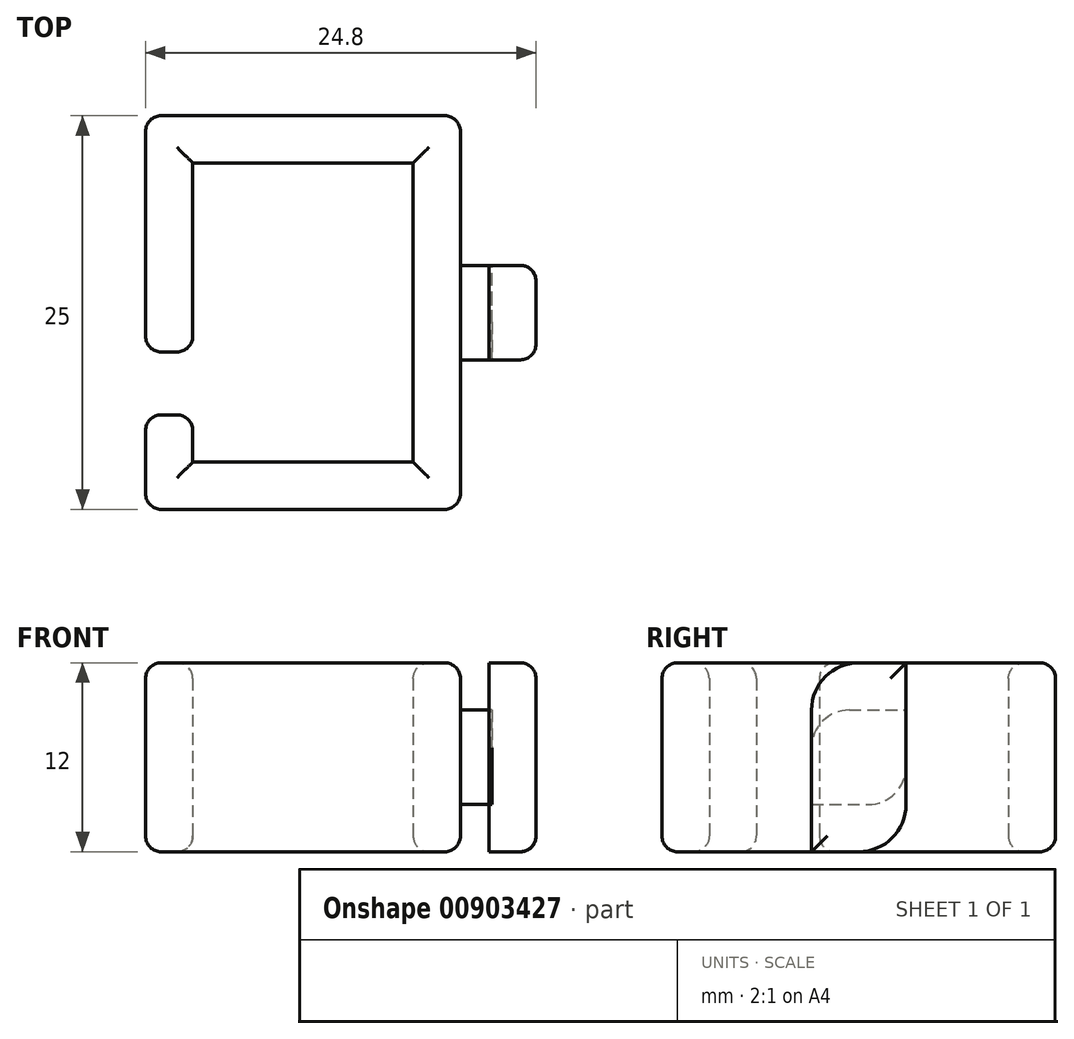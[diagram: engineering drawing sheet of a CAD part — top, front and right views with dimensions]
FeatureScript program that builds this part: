
annotation { "Feature Type Name" : "Feature", "Feature Type Description" : "" }
export const myFeature = defineFeature(function(context is Context, id is Id, definition is map)
    precondition{}
    {
        {
            var Q0;
            Q0=qCreatedBy(makeId("Right.planeOp"),FACE);
            var sketch = newSketch(context, id + "F0", { "sketchPlane" : qUnion([Q0])});
            skLineSegment(sketch, "E0.bottom", {"start": v(-3, -3) * mm, "end": v(3, -3) * mm});
            skLineSegment(sketch, "E0.top", {"start": v(-3, 3) * mm, "end": v(3, 3) * mm});
            skLineSegment(sketch, "E0.left", {"start": v(-3, -3) * mm, "end": v(-3, 3) * mm});
            skLineSegment(sketch, "E0.right", {"start": v(3, -3) * mm, "end": v(3, 3) * mm});
            skPoint(sketch, "E0.middle", {"position": v(0, 0) * mm});
            skLineSegment(sketch, "E1.bottom", {"start": v(-12.5, 6) * mm, "end": v(12.5, 6) * mm});
            skLineSegment(sketch, "E1.top", {"start": v(-12.5, -6) * mm, "end": v(12.5, -6) * mm});
            skLineSegment(sketch, "E1.left", {"start": v(-12.5, 6) * mm, "end": v(-12.5, -6) * mm});
            skLineSegment(sketch, "E1.right", {"start": v(12.5, 6) * mm, "end": v(12.5, -6) * mm});
            skLineSegment(sketch, "E2.bottom", {"start": v(-3, 6) * mm, "end": v(3, 6) * mm});
            skLineSegment(sketch, "E2.top", {"start": v(-3, -6) * mm, "end": v(3, -6) * mm});
            skLineSegment(sketch, "E2.left", {"start": v(-3, 6) * mm, "end": v(-3, -6) * mm});
            skLineSegment(sketch, "E2.right", {"start": v(3, 6) * mm, "end": v(3, -6) * mm});
            skLineSegment(sketch, "E3.bottom", {"start": v(9.5, 6) * mm, "end": v(-9.5, 6) * mm});
            skLineSegment(sketch, "E3.top", {"start": v(9.5, -6) * mm, "end": v(-9.5, -6) * mm});
            skLineSegment(sketch, "E3.left", {"start": v(9.5, 6) * mm, "end": v(9.5, -6) * mm});
            skLineSegment(sketch, "E3.right", {"start": v(-9.5, 6) * mm, "end": v(-9.5, -6) * mm});
            skSolve(sketch);
        }
        {
            var Q0;
            {var subQ2=sQuery(id+"F0.wireOp",EDGE,"E1.left");Q0=makeQuery(id+"F0.imprint","IMPRINT",FACE,{"disambiguationData":[TD([[makeQuery(id+"F0.imprint","IMPRINT",EDGE,{"derivedFrom":subQ2}),1.0]])]});}
            var Q1;
            {var subQ0=sQuery(id+"F0.wireOp",EDGE,"E0.top");Q1=makeQuery(id+"F0.imprint","IMPRINT",FACE,{"disambiguationData":[TD([[makeQuery(id+"F0.imprint","IMPRINT",EDGE,{"derivedFrom":subQ0}),1.0]])]});}
            var Q2;
            {var subQ0=sQuery(id+"F0.wireOp",EDGE,"E0.bottom");Q2=makeQuery(id+"F0.imprint","IMPRINT",FACE,{"disambiguationData":[TD([[makeQuery(id+"F0.imprint","IMPRINT",EDGE,{"derivedFrom":subQ0}),-1.0]])]});}
            var Q3;
            Q3=makeQuery(id+"F0.imprint","IMPRINT",FACE,{"disambiguationData":[TD([[makeQuery(id+"F0.imprint","IMPRINT",EDGE,{"derivedFrom":sQuery(id+"F0.wireOp",EDGE,"E0.bottom")}),1.0]])]});
            var Q4;
            {var subQ0=sQuery(id+"F0.wireOp",EDGE,"E1.right");Q4=makeQuery(id+"F0.imprint","IMPRINT",FACE,{"disambiguationData":[TD([[makeQuery(id+"F0.imprint","IMPRINT",EDGE,{"derivedFrom":subQ0}),-1.0]])]});}
            var Q5;
            {var subQ1=sQuery(id+"F0.wireOp",EDGE,"E0.left");Q5=makeQuery(id+"F0.imprint","IMPRINT",FACE,{"disambiguationData":[TD([[makeQuery(id+"F0.imprint","IMPRINT",EDGE,{"derivedFrom":subQ1}),1.0]])]});}
            var Q6;
            {var subQ6=sQuery(id+"F0.wireOp",EDGE,"E0.right");Q6=makeQuery(id+"F0.imprint","IMPRINT",FACE,{"disambiguationData":[TD([[makeQuery(id+"F0.imprint","IMPRINT",EDGE,{"derivedFrom":subQ6}),-1.0]])]});}
            extrude(context, id + "F1", {"entities" : qUnion([Q0, Q1, Q2, Q3, Q4, Q5, Q6]), "depth" : -3 * mm, "offsetDistance" : 25 * mm});
        }
        {
            var Q0;
            {var subQ0=sQuery(id+"F0.wireOp",EDGE,"E0.top");Q0=makeQuery(id+"F0.imprint","IMPRINT",FACE,{"disambiguationData":[TD([[makeQuery(id+"F0.imprint","IMPRINT",EDGE,{"derivedFrom":subQ0}),1.0]])]});}
            var Q1;
            Q1=makeQuery(id+"F0.imprint","IMPRINT",FACE,{"disambiguationData":[TD([[makeQuery(id+"F0.imprint","IMPRINT",EDGE,{"derivedFrom":sQuery(id+"F0.wireOp",EDGE,"E0.bottom")}),1.0]])]});
            var Q2;
            {var subQ0=sQuery(id+"F0.wireOp",EDGE,"E0.bottom");Q2=makeQuery(id+"F0.imprint","IMPRINT",FACE,{"disambiguationData":[TD([[makeQuery(id+"F0.imprint","IMPRINT",EDGE,{"derivedFrom":subQ0}),-1.0]])]});}
            extrude(context, id + "F2", {"entities" : qUnion([Q0, Q1, Q2]), "depth" : 4.8 * mm, "offsetDistance" : 25 * mm, "hasSecondDirection" : true, "secondDirectionOppositeDirection" : true, "secondDirectionDepth" : -1.8 * mm});
        }
        {
            var Q0;
            Q0=makeQuery(id+"F0.imprint","IMPRINT",FACE,{"disambiguationData":[TD([[makeQuery(id+"F0.imprint","IMPRINT",EDGE,{"derivedFrom":sQuery(id+"F0.wireOp",EDGE,"E0.bottom")}),1.0]])]});
            extrude(context, id + "F3", {"entities" : qUnion([Q0]), "depth" : 2 * mm, "offsetDistance" : 25 * mm});
        }
        {
            var Q0;
            {var subQ0=sQuery(id+"F0.wireOp",EDGE,"E1.right");Q0=makeQuery(id+"F0.imprint","IMPRINT",FACE,{"disambiguationData":[TD([[makeQuery(id+"F0.imprint","IMPRINT",EDGE,{"derivedFrom":subQ0}),-1.0]])]});}
            var Q1;
            {var subQ2=sQuery(id+"F0.wireOp",EDGE,"E1.left");Q1=makeQuery(id+"F0.imprint","IMPRINT",FACE,{"disambiguationData":[TD([[makeQuery(id+"F0.imprint","IMPRINT",EDGE,{"derivedFrom":subQ2}),1.0]])]});}
            extrude(context, id + "F4", {"entities" : qUnion([Q0, Q1]), "operationType" : NewBodyOperationType.ADD, "depth" : -20 * mm, "offsetDistance" : 25 * mm, "hasSecondDirection" : true, "secondDirectionOppositeDirection" : true, "secondDirectionDepth" : 3 * mm});
        }
        {
            var Q0;
            Q0=makeQuery(id+"F2.opExtrude","SWEPT_EDGE",EDGE,{"disambiguationData":[OSD([sQuery(id+"F0.wireOp",EDGE,"E1.bottom"),sQuery(id+"F0.wireOp",EDGE,"E2.left")])]});
            var Q1;
            Q1=makeQuery(id+"F2.opExtrude","SWEPT_EDGE",EDGE,{"disambiguationData":[OSD([sQuery(id+"F0.wireOp",EDGE,"E1.top"),sQuery(id+"F0.wireOp",EDGE,"E2.right")])]});
            fillet(context, id + "F5", {"entities" : qUnion([Q0, Q1]), "radius" : 3 * mm, "tangentPropagation" : true, "allowEdgeOverflow" : false});
        }
        {
            var Q0;
            Q0=makeQuery(id+"F3.opExtrude","SWEPT_EDGE",EDGE,{"disambiguationData":[OSD([sQuery(id+"F0.wireOp",EDGE,"E0.bottom"),sQuery(id+"F0.wireOp",EDGE,"E0.right"),sQuery(id+"F0.wireOp",EDGE,"E2.right")])]});
            var Q1;
            Q1=makeQuery(id+"F3.opExtrude","SWEPT_EDGE",EDGE,{"disambiguationData":[OSD([sQuery(id+"F0.wireOp",EDGE,"E0.top"),sQuery(id+"F0.wireOp",EDGE,"E0.left"),sQuery(id+"F0.wireOp",EDGE,"E2.left")])]});
            fillet(context, id + "F6", {"entities" : qUnion([Q0, Q1]), "radius" : 2.4 * mm, "tangentPropagation" : true, "allowEdgeOverflow" : false});
        }
        {
            var Q0;
            Q0=makeQuery(id+"F2.opExtrude","CAP_EDGE",EDGE,{"disambiguationData":[OSD([sQuery(id+"F0.wireOp",EDGE,"E0.right"),sQuery(id+"F0.wireOp",EDGE,"E2.right")])],"isStart":false});
            var Q1;
            Q1=makeQuery(id+"F2.opExtrude","CAP_EDGE",EDGE,{"disambiguationData":[OSD([sQuery(id+"F0.wireOp",EDGE,"E2.bottom")])],"isStart":false});
            var Q2;
            Q2=makeQuery(id+"F2.opExtrude","CAP_FACE",FACE,{"disambiguationData":[OSD([sQuery(id+"F0.wireOp",EDGE,"E0.left"),sQuery(id+"F0.wireOp",EDGE,"E0.right"),sQuery(id+"F0.wireOp",EDGE,"E1.bottom"),sQuery(id+"F0.wireOp",EDGE,"E1.top"),sQuery(id+"F0.wireOp",EDGE,"E2.left"),sQuery(id+"F0.wireOp",EDGE,"E2.right")])],"isStart":false});
            fillet(context, id + "F7", {"entities" : qUnion([Q0, Q1, Q2]), "radius" : 1 * mm, "tangentPropagation" : true, "allowEdgeOverflow" : false});
        }
        {
            var Q0;
            Q0=makeQuery(id+"F1.opExtrude","CAP_EDGE",EDGE,{"disambiguationData":[OSD([sQuery(id+"F0.wireOp",EDGE,"E1.left")])],"isStart":true});
            var Q1;
            Q1=makeQuery(id+"F1.opExtrude","CAP_EDGE",EDGE,{"disambiguationData":[OSD([sQuery(id+"F0.wireOp",EDGE,"E1.bottom")])],"isStart":true});
            var Q2;
            Q2=makeQuery(id+"F1.opExtrude","CAP_EDGE",EDGE,{"disambiguationData":[OSD([sQuery(id+"F0.wireOp",EDGE,"E1.top")])],"isStart":true});
            var Q3;
            Q3=makeQuery(id+"F1.opExtrude","CAP_EDGE",EDGE,{"disambiguationData":[OSD([sQuery(id+"F0.wireOp",EDGE,"E1.right")])],"isStart":true});
            var Q4;
            {var subQ0=sQuery(id+"F0.wireOp",EDGE,"E1.left");var subQ1=sQuery(id+"F0.wireOp",EDGE,"E1.top");Q4=makeQuery(id+"F4.boolean.opBoolean","MERGE",EDGE,{"derivedFrom":[makeQuery(id+"F1.opExtrude","SWEPT_EDGE",EDGE,{"disambiguationData":[OSD([subQ1,subQ0])]}),makeQuery(id+"F4.opExtrude","SWEPT_EDGE",EDGE,{"disambiguationData":[OSD([subQ1,subQ0])]})]});}
            var Q5;
            {var subQ0=sQuery(id+"F0.wireOp",EDGE,"E1.left");var subQ1=sQuery(id+"F0.wireOp",EDGE,"E1.bottom");Q5=makeQuery(id+"F4.boolean.opBoolean","MERGE",EDGE,{"derivedFrom":[makeQuery(id+"F1.opExtrude","SWEPT_EDGE",EDGE,{"disambiguationData":[OSD([subQ1,subQ0])]}),makeQuery(id+"F4.opExtrude","SWEPT_EDGE",EDGE,{"disambiguationData":[OSD([subQ1,subQ0])]})]});}
            var Q6;
            {var subQ0=sQuery(id+"F0.wireOp",EDGE,"E1.right");var subQ1=sQuery(id+"F0.wireOp",EDGE,"E1.bottom");Q6=makeQuery(id+"F4.boolean.opBoolean","MERGE",EDGE,{"derivedFrom":[makeQuery(id+"F1.opExtrude","SWEPT_EDGE",EDGE,{"disambiguationData":[OSD([subQ1,subQ0])]}),makeQuery(id+"F4.opExtrude","SWEPT_EDGE",EDGE,{"disambiguationData":[OSD([subQ1,subQ0])]})]});}
            var Q7;
            {var subQ0=sQuery(id+"F0.wireOp",EDGE,"E1.right");var subQ1=sQuery(id+"F0.wireOp",EDGE,"E1.top");Q7=makeQuery(id+"F4.boolean.opBoolean","MERGE",EDGE,{"derivedFrom":[makeQuery(id+"F1.opExtrude","SWEPT_EDGE",EDGE,{"disambiguationData":[OSD([subQ1,subQ0])]}),makeQuery(id+"F4.opExtrude","SWEPT_EDGE",EDGE,{"disambiguationData":[OSD([subQ1,subQ0])]})]});}
            fillet(context, id + "F8", {"entities" : qUnion([Q0, Q1, Q2, Q3, Q4, Q5, Q6, Q7]), "radius" : 1 * mm, "tangentPropagation" : true, "allowEdgeOverflow" : false});
        }
        {
            var Q0;
            Q0=makeQuery(id+"F4.opExtrude","SWEPT_FACE",FACE,{"disambiguationData":[OSD([sQuery(id+"F0.wireOp",EDGE,"E3.left")])]});
            var sketch = newSketch(context, id + "F9", { "sketchPlane" : qUnion([Q0])});
            skLineSegment(sketch, "E4.bottom", {"start": v(-20, -6) * mm, "end": v(14, -6) * mm});
            skLineSegment(sketch, "E4.top", {"start": v(-20, 18) * mm, "end": v(14, 18) * mm});
            skLineSegment(sketch, "E4.left", {"start": v(-20, -6) * mm, "end": v(-20, 18) * mm});
            skLineSegment(sketch, "E4.right", {"start": v(14, -6) * mm, "end": v(14, 18) * mm});
            skPoint(sketch, "E4.middle", {"position": v(-3, 6) * mm});
            skLineSegment(sketch, "E5.bottom", {"start": v(-17, 24.04) * mm, "end": v(11, 24.04) * mm});
            skLineSegment(sketch, "E5.top", {"start": v(-17, -12.04) * mm, "end": v(11, -12.04) * mm});
            skLineSegment(sketch, "E5.left", {"start": v(-17, 24.04) * mm, "end": v(-17, -12.04) * mm});
            skLineSegment(sketch, "E5.right", {"start": v(11, 24.04) * mm, "end": v(11, -12.04) * mm});
            skSolve(sketch);
        }
        {
            var Q0;
            {var subQ0=sQuery(id+"F9.wireOp",EDGE,"E4.left");var subQ1=sQuery(id+"F9.wireOp",EDGE,"E4.bottom");var subQ2=makeQuery(id+"F9.imprint","INTERSECT",VERTEX,{"derivedFrom":[subQ1,subQ0]});Q0=makeQuery(id+"F9.imprint","IMPRINT",FACE,{"disambiguationData":[TD([[makeQuery(id+"F9.imprint","IMPRINT",EDGE,{"disambiguationData":[TD([[subQ2,-1.0]])],"derivedFrom":subQ1}),1.0]])]});}
            extrude(context, id + "F10", {"entities" : qUnion([Q0]), "operationType" : NewBodyOperationType.ADD, "depth" : 12 * mm, "offsetDistance" : 25 * mm});
        }
        {
            var Q0;
            Q0=makeQuery(id+"F10.opExtrude","CAP_FACE",FACE,{"disambiguationData":[OSD([sQuery(id+"F0.wireOp",EDGE,"E1.bottom"),sQuery(id+"F0.wireOp",EDGE,"E3.left"),sQuery(id+"F9.wireOp",EDGE,"E4.bottom"),sQuery(id+"F9.wireOp",EDGE,"E4.left"),sQuery(id+"F9.wireOp",EDGE,"E5.left")])],"isStart":false});
            extrude(context, id + "F11", {"entities" : qUnion([Q0]), "operationType" : NewBodyOperationType.ADD, "depth" : 7 * mm, "offsetDistance" : 25 * mm, "hasSecondDirection" : true, "secondDirectionOppositeDirection" : true, "secondDirectionDepth" : -4 * mm});
        }
        {
            var Q0;
            Q0=makeQuery(id+"F4.opExtrude","CAP_EDGE",EDGE,{"disambiguationData":[OSD([sQuery(id+"F0.wireOp",EDGE,"E1.left")])],"isStart":false});
            var Q1;
            {var subQ0=sQuery(id+"F0.wireOp",EDGE,"E1.bottom");Q1=makeQuery(id+"F11.boolean.opBoolean","MERGE",EDGE,{"derivedFrom":[makeQuery(id+"F4.opExtrude","CAP_EDGE",EDGE,{"disambiguationData":[OSD([subQ0]),TDD([makeQuery(id+"F0.imprint","IMPRINT",EDGE,{"disambiguationData":[TD([[makeQuery(id+"F0.imprint","INTERSECT",VERTEX,{"derivedFrom":[subQ0,sQuery(id+"F0.wireOp",EDGE,"E3.right")]}),1.0]])],"derivedFrom":subQ0})])],"isStart":false}),makeQuery(id+"F11.opExtrude","SWEPT_EDGE",EDGE,{"disambiguationData":[OSD([subQ0,sQuery(id+"F0.wireOp",EDGE,"E3.left"),sQuery(id+"F9.wireOp",EDGE,"E4.left")])]})]});}
            var Q2;
            {var subQ0=sQuery(id+"F0.wireOp",EDGE,"E1.left");var subQ1=sQuery(id+"F0.wireOp",EDGE,"E1.bottom");Q2=makeQuery(id+"F8.opFillet","BLEND_EDGE",EDGE,{"blendedFrom":[makeQuery(id+"F4.boolean.opBoolean","MERGE",EDGE,{"derivedFrom":[makeQuery(id+"F1.opExtrude","SWEPT_EDGE",EDGE,{"disambiguationData":[OSD([subQ1,subQ0])]}),makeQuery(id+"F4.opExtrude","SWEPT_EDGE",EDGE,{"disambiguationData":[OSD([subQ1,subQ0])]})]}),makeQuery(id+"F4.opExtrude","CAP_FACE",FACE,{"disambiguationData":[OSD([subQ1,sQuery(id+"F0.wireOp",EDGE,"E1.top"),subQ0,sQuery(id+"F0.wireOp",EDGE,"E3.right")])],"isStart":false})],"blendedInto":[makeQuery(id+"F4.opExtrude","CAP_FACE",FACE,{"disambiguationData":[OSD([subQ1,sQuery(id+"F0.wireOp",EDGE,"E1.top"),subQ0,sQuery(id+"F0.wireOp",EDGE,"E3.right")])],"isStart":false})]});}
            var Q3;
            {var subQ0=sQuery(id+"F0.wireOp",EDGE,"E1.top");Q3=makeQuery(id+"F11.boolean.opBoolean","MERGE",EDGE,{"derivedFrom":[makeQuery(id+"F4.opExtrude","CAP_EDGE",EDGE,{"disambiguationData":[OSD([subQ0]),TDD([makeQuery(id+"F0.imprint","IMPRINT",EDGE,{"disambiguationData":[TD([[makeQuery(id+"F0.imprint","INTERSECT",VERTEX,{"derivedFrom":[subQ0,sQuery(id+"F0.wireOp",EDGE,"E1.left")]}),-1.0]])],"derivedFrom":subQ0})])],"isStart":false}),makeQuery(id+"F11.opExtrude","SWEPT_EDGE",EDGE,{"disambiguationData":[OSD([sQuery(id+"F9.wireOp",EDGE,"E4.bottom"),sQuery(id+"F9.wireOp",EDGE,"E4.left")])]})]});}
            var Q4;
            Q4=makeQuery(id+"F11.opExtrude","CAP_EDGE",EDGE,{"disambiguationData":[OSD([sQuery(id+"F9.wireOp",EDGE,"E4.left")])],"isStart":true});
            var Q5;
            {var subQ0=sQuery(id+"F0.wireOp",EDGE,"E1.left");var subQ1=sQuery(id+"F0.wireOp",EDGE,"E1.top");Q5=makeQuery(id+"F8.opFillet","BLEND_EDGE",EDGE,{"blendedFrom":[makeQuery(id+"F4.boolean.opBoolean","MERGE",EDGE,{"derivedFrom":[makeQuery(id+"F1.opExtrude","SWEPT_EDGE",EDGE,{"disambiguationData":[OSD([subQ1,subQ0])]}),makeQuery(id+"F4.opExtrude","SWEPT_EDGE",EDGE,{"disambiguationData":[OSD([subQ1,subQ0])]})]}),makeQuery(id+"F4.opExtrude","CAP_FACE",FACE,{"disambiguationData":[OSD([sQuery(id+"F0.wireOp",EDGE,"E1.bottom"),subQ1,subQ0,sQuery(id+"F0.wireOp",EDGE,"E3.right")])],"isStart":false})],"blendedInto":[makeQuery(id+"F4.opExtrude","CAP_FACE",FACE,{"disambiguationData":[OSD([sQuery(id+"F0.wireOp",EDGE,"E1.bottom"),subQ1,subQ0,sQuery(id+"F0.wireOp",EDGE,"E3.right")])],"isStart":false})]});}
            var Q6;
            {var subQ0=sQuery(id+"F0.wireOp",EDGE,"E3.left");var subQ1=sQuery(id+"F0.wireOp",EDGE,"E1.bottom");Q6=makeQuery(id+"F10.boolean.opBoolean","MERGE",EDGE,{"derivedFrom":[makeQuery(id+"F4.opExtrude","CAP_EDGE",EDGE,{"disambiguationData":[OSD([subQ1]),TDD([makeQuery(id+"F0.imprint","IMPRINT",EDGE,{"disambiguationData":[TD([[makeQuery(id+"F0.imprint","INTERSECT",VERTEX,{"derivedFrom":[subQ1,sQuery(id+"F0.wireOp",EDGE,"E1.right")]}),1.0]])],"derivedFrom":subQ1})])],"isStart":false}),makeQuery(id+"F10.opExtrude","SWEPT_EDGE",EDGE,{"disambiguationData":[OSD([subQ1,subQ0,sQuery(id+"F9.wireOp",EDGE,"E4.left")])]})]});}
            var Q7;
            Q7=makeQuery(id+"F10.opExtrude","CAP_EDGE",EDGE,{"disambiguationData":[OSD([sQuery(id+"F9.wireOp",EDGE,"E4.left")])],"isStart":false});
            var Q8;
            Q8=makeQuery(id+"F10.opExtrude","CAP_EDGE",EDGE,{"disambiguationData":[OSD([sQuery(id+"F9.wireOp",EDGE,"E4.bottom")])],"isStart":false});
            var Q9;
            Q9=makeQuery(id+"F10.opExtrude","CAP_EDGE",EDGE,{"disambiguationData":[OSD([sQuery(id+"F0.wireOp",EDGE,"E1.bottom"),sQuery(id+"F0.wireOp",EDGE,"E3.left")])],"isStart":false});
            var Q10;
            Q10=makeQuery(id+"F10.opExtrude","CAP_EDGE",EDGE,{"disambiguationData":[OSD([sQuery(id+"F9.wireOp",EDGE,"E5.left")])],"isStart":false});
            var Q11;
            Q11=makeQuery(id+"F11.opExtrude","CAP_EDGE",EDGE,{"disambiguationData":[OSD([sQuery(id+"F0.wireOp",EDGE,"E1.bottom"),sQuery(id+"F0.wireOp",EDGE,"E3.left")])],"isStart":true});
            var Q12;
            Q12=makeQuery(id+"F11.opExtrude","SWEPT_EDGE",EDGE,{"disambiguationData":[OSD([sQuery(id+"F0.wireOp",EDGE,"E1.bottom"),sQuery(id+"F0.wireOp",EDGE,"E3.left"),sQuery(id+"F9.wireOp",EDGE,"E5.left")])]});
            var Q13;
            Q13=makeQuery(id+"F10.opExtrude","SWEPT_EDGE",EDGE,{"disambiguationData":[OSD([sQuery(id+"F0.wireOp",EDGE,"E1.bottom"),sQuery(id+"F0.wireOp",EDGE,"E3.left"),sQuery(id+"F9.wireOp",EDGE,"E5.left")])]});
            var Q14;
            Q14=makeQuery(id+"F4.opExtrude","SWEPT_EDGE",EDGE,{"disambiguationData":[OSD([sQuery(id+"F0.wireOp",EDGE,"E1.bottom"),sQuery(id+"F0.wireOp",EDGE,"E3.left")])]});
            var Q15;
            Q15=makeQuery(id+"F1.opExtrude","CAP_EDGE",EDGE,{"disambiguationData":[OSD([sQuery(id+"F0.wireOp",EDGE,"E1.bottom")])],"isStart":false});
            var Q16;
            Q16=makeQuery(id+"F4.opExtrude","SWEPT_EDGE",EDGE,{"disambiguationData":[OSD([sQuery(id+"F0.wireOp",EDGE,"E1.bottom"),sQuery(id+"F0.wireOp",EDGE,"E3.right")])]});
            var Q17;
            {var subQ0=sQuery(id+"F0.wireOp",EDGE,"E1.right");var subQ1=sQuery(id+"F0.wireOp",EDGE,"E1.top");Q17=makeQuery(id+"F8.opFillet","BLEND_EDGE",EDGE,{"blendedFrom":[makeQuery(id+"F4.boolean.opBoolean","MERGE",EDGE,{"derivedFrom":[makeQuery(id+"F1.opExtrude","SWEPT_EDGE",EDGE,{"disambiguationData":[OSD([subQ1,subQ0])]}),makeQuery(id+"F4.opExtrude","SWEPT_EDGE",EDGE,{"disambiguationData":[OSD([subQ1,subQ0])]})]}),makeQuery(id+"F4.opExtrude","CAP_FACE",FACE,{"disambiguationData":[OSD([sQuery(id+"F0.wireOp",EDGE,"E1.bottom"),subQ1,subQ0,sQuery(id+"F0.wireOp",EDGE,"E3.left")])],"isStart":false})],"blendedInto":[makeQuery(id+"F4.opExtrude","CAP_FACE",FACE,{"disambiguationData":[OSD([sQuery(id+"F0.wireOp",EDGE,"E1.bottom"),subQ1,subQ0,sQuery(id+"F0.wireOp",EDGE,"E3.left")])],"isStart":false})]});}
            var Q18;
            {var subQ0=sQuery(id+"F0.wireOp",EDGE,"E1.top");Q18=makeQuery(id+"F10.boolean.opBoolean","MERGE",EDGE,{"derivedFrom":[makeQuery(id+"F4.opExtrude","CAP_EDGE",EDGE,{"disambiguationData":[OSD([subQ0]),TDD([makeQuery(id+"F0.imprint","IMPRINT",EDGE,{"disambiguationData":[TD([[makeQuery(id+"F0.imprint","INTERSECT",VERTEX,{"derivedFrom":[subQ0,sQuery(id+"F0.wireOp",EDGE,"E1.right")]}),1.0]])],"derivedFrom":subQ0})])],"isStart":false}),makeQuery(id+"F10.opExtrude","SWEPT_EDGE",EDGE,{"disambiguationData":[OSD([sQuery(id+"F9.wireOp",EDGE,"E4.bottom"),sQuery(id+"F9.wireOp",EDGE,"E4.left")])]})]});}
            var Q19;
            Q19=makeQuery(id+"F4.opExtrude","CAP_EDGE",EDGE,{"disambiguationData":[OSD([sQuery(id+"F0.wireOp",EDGE,"E1.right")])],"isStart":false});
            var Q20;
            {var subQ0=sQuery(id+"F0.wireOp",EDGE,"E1.right");var subQ1=sQuery(id+"F0.wireOp",EDGE,"E1.bottom");Q20=makeQuery(id+"F8.opFillet","BLEND_EDGE",EDGE,{"blendedFrom":[makeQuery(id+"F4.boolean.opBoolean","MERGE",EDGE,{"derivedFrom":[makeQuery(id+"F1.opExtrude","SWEPT_EDGE",EDGE,{"disambiguationData":[OSD([subQ1,subQ0])]}),makeQuery(id+"F4.opExtrude","SWEPT_EDGE",EDGE,{"disambiguationData":[OSD([subQ1,subQ0])]})]}),makeQuery(id+"F4.opExtrude","CAP_FACE",FACE,{"disambiguationData":[OSD([subQ1,sQuery(id+"F0.wireOp",EDGE,"E1.top"),subQ0,sQuery(id+"F0.wireOp",EDGE,"E3.left")])],"isStart":false})],"blendedInto":[makeQuery(id+"F4.opExtrude","CAP_FACE",FACE,{"disambiguationData":[OSD([subQ1,sQuery(id+"F0.wireOp",EDGE,"E1.top"),subQ0,sQuery(id+"F0.wireOp",EDGE,"E3.left")])],"isStart":false})]});}
            var Q21;
            Q21=makeQuery(id+"F11.opExtrude","CAP_EDGE",EDGE,{"disambiguationData":[OSD([sQuery(id+"F9.wireOp",EDGE,"E4.bottom")])],"isStart":true});
            var Q22;
            Q22=makeQuery(id+"F11.opExtrude","CAP_EDGE",EDGE,{"disambiguationData":[OSD([sQuery(id+"F9.wireOp",EDGE,"E5.left")])],"isStart":true});
            var Q23;
            Q23=makeQuery(id+"F4.opExtrude","SWEPT_EDGE",EDGE,{"disambiguationData":[OSD([sQuery(id+"F0.wireOp",EDGE,"E1.top"),sQuery(id+"F0.wireOp",EDGE,"E3.right")])]});
            var Q24;
            Q24=makeQuery(id+"F11.opExtrude","SWEPT_EDGE",EDGE,{"disambiguationData":[OSD([sQuery(id+"F9.wireOp",EDGE,"E4.bottom"),sQuery(id+"F9.wireOp",EDGE,"E5.left")])]});
            var Q25;
            Q25=makeQuery(id+"F1.opExtrude","CAP_EDGE",EDGE,{"disambiguationData":[OSD([sQuery(id+"F0.wireOp",EDGE,"E1.top")])],"isStart":false});
            var Q26;
            Q26=makeQuery(id+"F4.opExtrude","SWEPT_EDGE",EDGE,{"disambiguationData":[OSD([sQuery(id+"F0.wireOp",EDGE,"E1.top"),sQuery(id+"F0.wireOp",EDGE,"E3.left")])]});
            var Q27;
            Q27=makeQuery(id+"F10.opExtrude","SWEPT_EDGE",EDGE,{"disambiguationData":[OSD([sQuery(id+"F9.wireOp",EDGE,"E4.bottom"),sQuery(id+"F9.wireOp",EDGE,"E5.left")])]});
            var Q28;
            Q28=makeQuery(id+"F11.opExtrude","CAP_EDGE",EDGE,{"disambiguationData":[OSD([sQuery(id+"F9.wireOp",EDGE,"E5.left")])],"isStart":false});
            var Q29;
            Q29=makeQuery(id+"F10.opExtrude","CAP_EDGE",EDGE,{"disambiguationData":[OSD([sQuery(id+"F9.wireOp",EDGE,"E5.left")])],"isStart":true});
            var Q30;
            Q30=makeQuery(id+"F4.opExtrude","CAP_EDGE",EDGE,{"disambiguationData":[OSD([sQuery(id+"F0.wireOp",EDGE,"E3.left")])],"isStart":true});
            var Q31;
            Q31=makeQuery(id+"F4.opExtrude","CAP_EDGE",EDGE,{"disambiguationData":[OSD([sQuery(id+"F0.wireOp",EDGE,"E3.right")])],"isStart":true});
            fillet(context, id + "F12", {"entities" : qUnion([Q0, Q1, Q2, Q3, Q4, Q5, Q6, Q7, Q8, Q9, Q10, Q11, Q12, Q13, Q14, Q15, Q16, Q17, Q18, Q19, Q20, Q21, Q22, Q23, Q24, Q25, Q26, Q27, Q28, Q29, Q30, Q31]), "radius" : 1 * mm, "tangentPropagation" : true, "allowEdgeOverflow" : false});
        }
    });
